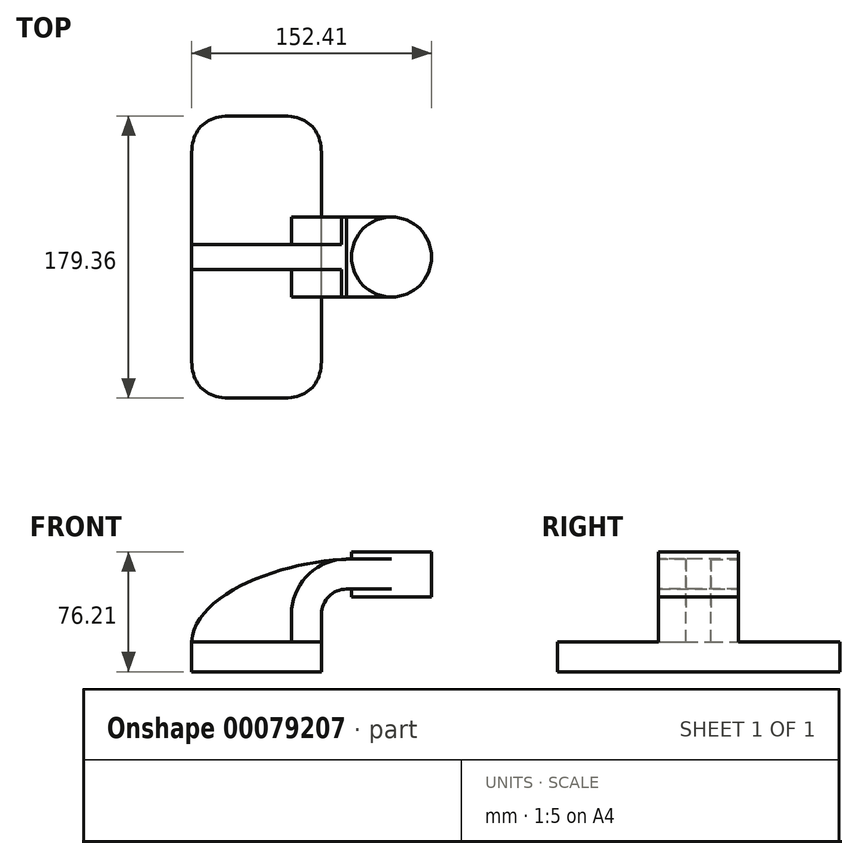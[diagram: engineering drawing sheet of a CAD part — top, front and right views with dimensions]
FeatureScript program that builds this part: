
annotation { "Feature Type Name" : "Feature", "Feature Type Description" : "" }
export const myFeature = defineFeature(function(context is Context, id is Id, definition is map)
    precondition{}
    {
        {
            var Q0;
            Q0=qCreatedBy(makeId("Front.planeOp"),FACE);
            var sketch = newSketch(context, id + "F0", { "sketchPlane" : qUnion([Q0])});
            skLineSegment(sketch, "E0.rect.bottom", {"start": v(-41.28, 9.52) * mm, "end": v(41.28, 9.52) * mm});
            skLineSegment(sketch, "E0.rect.top", {"start": v(-41.28, -9.52) * mm, "end": v(41.28, -9.52) * mm});
            skLineSegment(sketch, "E0.rect.left", {"start": v(-41.28, 9.52) * mm, "end": v(-41.28, -9.52) * mm});
            skLineSegment(sketch, "E0.rect.right", {"start": v(41.28, 9.52) * mm, "end": v(41.28, -9.52) * mm});
            skPoint(sketch, "E0.rect.middle", {"position": v(0, 0) * mm});
            skLineSegment(sketch, "E1", {"start": v(41.28, 9.52) * mm, "end": v(41.28, 27) * mm});
            skArc(sketch, "E2", {"start": v(41.28, 27) * mm, "mid": v(45.92, 38.23) * mm, "end": v(57.15, 42.88) * mm});
            skLineSegment(sketch, "E3", {"start": v(57.15, 42.88) * mm, "end": v(85.72, 42.88) * mm});
            skLineSegment(sketch, "E4.rect.bottom", {"start": v(60.32, 38.1) * mm, "end": v(111.12, 38.1) * mm});
            skLineSegment(sketch, "E4.rect.top", {"start": v(60.32, 66.68) * mm, "end": v(111.12, 66.68) * mm});
            skLineSegment(sketch, "E4.rect.left", {"start": v(60.32, 38.1) * mm, "end": v(60.32, 66.68) * mm});
            skLineSegment(sketch, "E4.rect.right", {"start": v(111.13, 38.1) * mm, "end": v(111.12, 66.68) * mm});
            skPoint(sketch, "E4.rect.middle", {"position": v(85.72, 52.39) * mm});
            skLineSegment(sketch, "E5.0", {"start": v(57.15, 61.93) * mm, "end": v(85.72, 61.93) * mm});
            skArc(sketch, "E5.1", {"start": v(22.23, 27) * mm, "mid": v(32.45, 51.7) * mm, "end": v(57.15, 61.93) * mm});
            skLineSegment(sketch, "E5.2", {"start": v(22.23, 9.52) * mm, "end": v(22.23, 27) * mm});
            skLineSegment(sketch, "E6", {"start": v(85.72, 38.1) * mm, "end": v(85.72, 66.68) * mm});
            skFitSpline(sketch, "E7", {"points": [v(-41.28, 9.53) * mm, v(57.15, 61.93) * mm], "startDerivative": vector(5.2, 92.34) * mm, "endDerivative": vector(120.92, 4.22) * mm});
            skSolve(sketch);
        }
        {
            var Q0;
            Q0=makeQuery(id+"F0.imprint","IMPRINT",FACE,{"disambiguationData":[TD([[makeQuery(id+"F0.imprint","IMPRINT",EDGE,{"derivedFrom":sQuery(id+"F0.wireOp",EDGE,"E0.rect.top")}),1.0]])]});
            extrude(context, id + "F1", {"entities" : qUnion([Q0]), "endBound" : BoundingType.SYMMETRIC, "depth" : 179.36 * mm});
        }
        {
            var Q0;
            {var subQ9=sQuery(id+"F0.wireOp",EDGE,"E1");Q0=makeQuery(id+"F0.imprint","IMPRINT",FACE,{"disambiguationData":[TD([[makeQuery(id+"F0.imprint","IMPRINT",EDGE,{"derivedFrom":subQ9}),1.0]])]});}
            var Q1;
            {var subQ0=sQuery(id+"F0.wireOp",EDGE,"E6");var subQ1=sQuery(id+"F0.wireOp",EDGE,"E3");var subQ2=makeQuery(id+"F0.imprint","INTERSECT",VERTEX,{"derivedFrom":[subQ1,subQ0]});Q1=makeQuery(id+"F0.imprint","IMPRINT",FACE,{"disambiguationData":[TD([[makeQuery(id+"F0.imprint","IMPRINT",EDGE,{"disambiguationData":[TD([[subQ2,1.0]])],"derivedFrom":subQ1}),1.0]])]});}
            extrude(context, id + "F2", {"entities" : qUnion([Q0, Q1]), "operationType" : NewBodyOperationType.ADD, "endBound" : BoundingType.SYMMETRIC, "depth" : 50.8 * mm});
        }
        {
            var Q0;
            {var subQ3=sQuery(id+"F0.wireOp",EDGE,"E5.2");Q0=makeQuery(id+"F0.imprint","IMPRINT",FACE,{"disambiguationData":[TD([[makeQuery(id+"F0.imprint","IMPRINT",EDGE,{"derivedFrom":subQ3}),1.0]])]});}
            extrude(context, id + "F3", {"entities" : qUnion([Q0]), "operationType" : NewBodyOperationType.ADD, "endBound" : BoundingType.SYMMETRIC, "depth" : 15.88 * mm});
        }
        {
            var Q0;
            {var subQ5=sQuery(id+"F0.wireOp",EDGE,"E4.rect.right");Q0=makeQuery(id+"F0.imprint","IMPRINT",FACE,{"disambiguationData":[TD([[makeQuery(id+"F0.imprint","IMPRINT",EDGE,{"derivedFrom":subQ5}),1.0]])]});}
            var Q1;
            Q1=sQuery(id+"F0.wireOp",EDGE,"E6");
            revolve(context, id + "F4", {"operationType" : NewBodyOperationType.ADD, "entities" : qUnion([Q0]), "axis" : qUnion([Q1]), "revolveType" : RevolveType.FULL});
        }
        {
            var Q0;
            Q0=makeQuery(id+"F1.opExtrude","CAP_EDGE",EDGE,{"disambiguationData":[OSD([sQuery(id+"F0.wireOp",EDGE,"E0.rect.right")])],"isStart":false});
            var Q1;
            Q1=makeQuery(id+"F1.opExtrude","CAP_EDGE",EDGE,{"disambiguationData":[OSD([sQuery(id+"F0.wireOp",EDGE,"E0.rect.left")])],"isStart":false});
            var Q2;
            Q2=makeQuery(id+"F1.opExtrude","CAP_EDGE",EDGE,{"disambiguationData":[OSD([sQuery(id+"F0.wireOp",EDGE,"E0.rect.right")])],"isStart":true});
            var Q3;
            Q3=makeQuery(id+"F1.opExtrude","CAP_EDGE",EDGE,{"disambiguationData":[OSD([sQuery(id+"F0.wireOp",EDGE,"E0.rect.left")])],"isStart":true});
            fillet(context, id + "F5", {"entities" : qUnion([Q0, Q1, Q2, Q3]), "radius" : 25.4 * mm, "tangentPropagation" : true, "rho" : 0.5, "crossSection" : FilletCrossSection.CONIC, "allowEdgeOverflow" : false});
        }
    });
